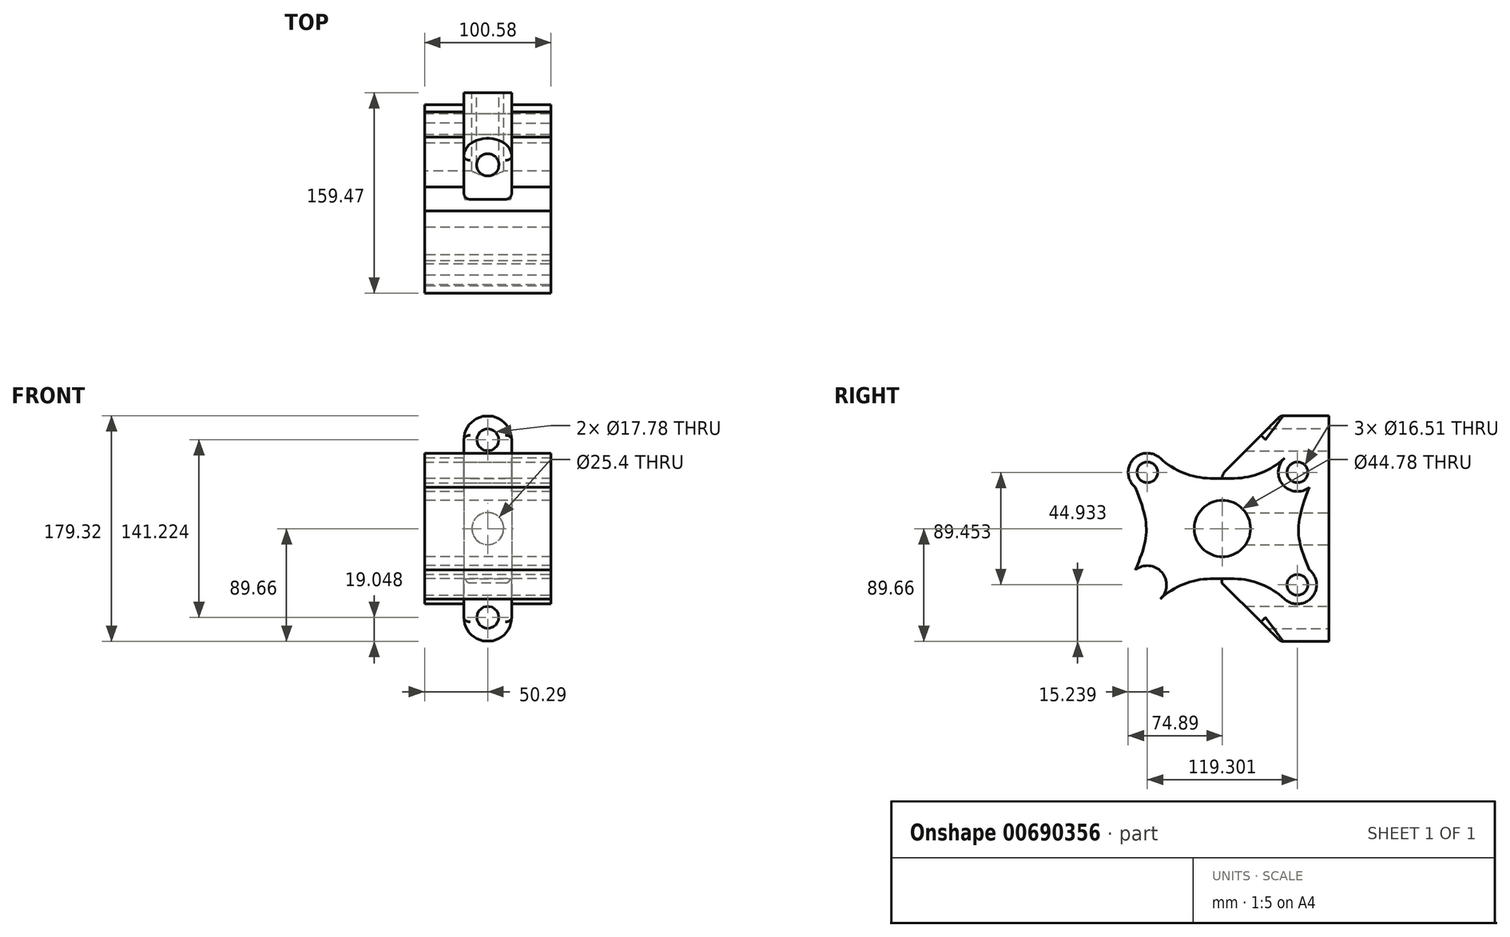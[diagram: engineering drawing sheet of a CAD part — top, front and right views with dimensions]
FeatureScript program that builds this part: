
annotation { "Feature Type Name" : "Feature", "Feature Type Description" : "" }
export const myFeature = defineFeature(function(context is Context, id is Id, definition is map)
    precondition{}
    {
        {
            var Q0;
            Q0=qCreatedBy(makeId("Right.planeOp"),FACE);
            var sketch = newSketch(context, id + "F0", { "sketchPlane" : qUnion([Q0])});
            skCircle(sketch, "E0", {"center": v(-59.65, 44.73) * mm, "radius": 15.24 * mm});
            skCircle(sketch, "E1.MirrorC", {"center": v(59.65, 44.73) * mm, "radius": 15.24 * mm});
            skCircle(sketch, "E2.MirrorC", {"center": v(59.65, -44.73) * mm, "radius": 15.24 * mm});
            skCircle(sketch, "E3.MirrorC", {"center": v(-59.65, -44.73) * mm, "radius": 15.24 * mm});
            skCircle(sketch, "E4", {"center": v(0, 0) * mm, "radius": 28.6 * mm});
            skCircle(sketch, "E5", {"center": v(0, 0) * mm, "radius": 22.4 * mm});
            skLineSegment(sketch, "E6.top", {"start": v(-9.5, 39.93) * mm, "end": v(15.9, 39.93) * mm});
            skArc(sketch, "E7", {"start": v(-49.3, 55.92) * mm, "mid": v(-30.87, 44.26) * mm, "end": v(-9.5, 39.93) * mm});
            skArc(sketch, "E8.MirrorCS", {"start": v(49.3, 55.92) * mm, "mid": v(30.87, 44.26) * mm, "end": v(9.5, 39.93) * mm});
            skArc(sketch, "E9.MirrorCS", {"start": v(49.3, -55.92) * mm, "mid": v(30.87, -44.26) * mm, "end": v(9.5, -39.93) * mm});
            skLineSegment(sketch, "E10.MirrorCS", {"start": v(-9.5, -39.93) * mm, "end": v(15.9, -39.93) * mm});
            skArc(sketch, "E11.MirrorCS", {"start": v(-49.3, -55.92) * mm, "mid": v(-30.87, -44.26) * mm, "end": v(-9.5, -39.93) * mm});
            skFitSpline(sketch, "E12", {"points": [v(69.2, 32.85) * mm, v(69.2, -32.84) * mm], "startDerivative": vector(-36.22, -89.62) * mm, "endDerivative": vector(33.53, -77.58) * mm});
            skFitSpline(sketch, "E13.MirrorCS", {"points": [v(-69.2, 32.85) * mm, v(-69.2, -32.84) * mm], "startDerivative": vector(36.22, -89.62) * mm, "endDerivative": vector(-33.53, -77.58) * mm});
            skPoint(sketch, "E6.left.start.orphan", {"position": v(-12.7, 65.76) * mm});
            skSolve(sketch);
        }
        {
            var Q0;
            Q0=qCreatedBy(makeId("Front.planeOp"),FACE);
            cPlane(context, id + "F1", {"entities" : qUnion([Q0]), "cplaneType" : CPlaneType.OFFSET, "offset" : 84.58 * mm, "oppositeDirection" : true, "width" : 152.4 * mm, "height" : 152.4 * mm});
        }
        {
            var Q0;
            Q0=qCreatedBy(id+"F1.planeOp",FACE);
            var sketch = newSketch(context, id + "F2", { "sketchPlane" : qUnion([Q0])});
            skArc(sketch, "E14", {"start": v(19.05, 70.61) * mm, "mid": v(0, 89.66) * mm, "end": v(-19.05, 70.61) * mm});
            skCircle(sketch, "E15", {"center": v(0, 0) * mm, "radius": 12.7 * mm});
            skArc(sketch, "E16", {"start": v(-19.05, -70.61) * mm, "mid": v(0, -89.66) * mm, "end": v(19.05, -70.61) * mm});
            skLineSegment(sketch, "E17", {"start": v(19.05, 70.61) * mm, "end": v(19.05, -70.61) * mm});
            skLineSegment(sketch, "E18", {"start": v(-19.05, 70.61) * mm, "end": v(-19.05, -70.61) * mm});
            skCircle(sketch, "E19", {"center": v(0, 70.61) * mm, "radius": 8.9 * mm});
            skCircle(sketch, "E20", {"center": v(0, -70.61) * mm, "radius": 8.9 * mm});
            skSolve(sketch);
        }
        {
            var Q0;
            Q0=makeQuery(id+"F0.imprint","IMPRINT",FACE,{"disambiguationData":[TD([[makeQuery(id+"F0.imprint","IMPRINT",EDGE,{"derivedFrom":sQuery(id+"F0.wireOp",EDGE,"E4")}),-1.0]])]});
            var Q1;
            {var subQ0=sQuery(id+"F0.wireOp",EDGE,"E0");var subQ1=makeQuery(id+"F0.imprint","INTERSECT",VERTEX,{"derivedFrom":[subQ0,sQuery(id+"F0.wireOp",EDGE,"E7")]});Q1=makeQuery(id+"F0.imprint","IMPRINT",FACE,{"disambiguationData":[TD([[makeQuery(id+"F0.imprint","IMPRINT",EDGE,{"disambiguationData":[TD([[subQ1,-1.0]])],"derivedFrom":subQ0}),1.0]])]});}
            var Q2;
            {var subQ0=sQuery(id+"F0.wireOp",EDGE,"E3.MirrorC");var subQ1=makeQuery(id+"F0.imprint","INTERSECT",VERTEX,{"derivedFrom":[subQ0,sQuery(id+"F0.wireOp",EDGE,"E11.MirrorCS")]});Q2=makeQuery(id+"F0.imprint","IMPRINT",FACE,{"disambiguationData":[TD([[makeQuery(id+"F0.imprint","IMPRINT",EDGE,{"disambiguationData":[TD([[subQ1,-1.0]])],"derivedFrom":subQ0}),-1.0]])]});}
            var Q3;
            {var subQ0=sQuery(id+"F0.wireOp",EDGE,"E1.MirrorC");var subQ1=makeQuery(id+"F0.imprint","INTERSECT",VERTEX,{"derivedFrom":[subQ0,sQuery(id+"F0.wireOp",EDGE,"E8.MirrorCS")]});Q3=makeQuery(id+"F0.imprint","IMPRINT",FACE,{"disambiguationData":[TD([[makeQuery(id+"F0.imprint","IMPRINT",EDGE,{"disambiguationData":[TD([[subQ1,-1.0]])],"derivedFrom":subQ0}),-1.0]])]});}
            var Q4;
            {var subQ0=sQuery(id+"F0.wireOp",EDGE,"E2.MirrorC");var subQ1=makeQuery(id+"F0.imprint","INTERSECT",VERTEX,{"derivedFrom":[sQuery(id+"F0.wireOp",EDGE,"E9.MirrorCS"),subQ0]});Q4=makeQuery(id+"F0.imprint","IMPRINT",FACE,{"disambiguationData":[TD([[makeQuery(id+"F0.imprint","IMPRINT",EDGE,{"disambiguationData":[TD([[subQ1,-1.0]])],"derivedFrom":subQ0}),1.0]])]});}
            var Q5;
            Q5=makeQuery(id+"F0.imprint","IMPRINT",FACE,{"disambiguationData":[TD([[makeQuery(id+"F0.imprint","IMPRINT",EDGE,{"derivedFrom":sQuery(id+"F0.wireOp",EDGE,"E4")}),1.0]])]});
            extrude(context, id + "F3", {"entities" : qUnion([Q0, Q1, Q2, Q3, Q4, Q5]), "endBound" : BoundingType.SYMMETRIC, "depth" : 100.58 * mm, "offsetDistance" : 25.4 * mm});
        }
        {
            var Q0;
            Q0=makeQuery(id+"F2.imprint","IMPRINT",FACE,{"disambiguationData":[TD([[makeQuery(id+"F2.imprint","IMPRINT",EDGE,{"derivedFrom":sQuery(id+"F2.wireOp",EDGE,"E14")}),1.0]])]});
            extrude(context, id + "F4", {"entities" : qUnion([Q0]), "operationType" : NewBodyOperationType.ADD, "depth" : 84.84 * mm, "offsetDistance" : 25.4 * mm});
        }
        {
            var Q0;
            Q0=qCreatedBy(makeId("Right.planeOp"),FACE);
            var sketch = newSketch(context, id + "F5", { "sketchPlane" : qUnion([Q0])});
            skLineSegment(sketch, "E21", {"start": v(-2.45, 41) * mm, "end": v(-2.45, 96.5) * mm});
            skLineSegment(sketch, "E22", {"start": v(-2.45, 96.5) * mm, "end": v(53.05, 96.5) * mm});
            skLineSegment(sketch, "E23", {"start": v(53.05, 96.5) * mm, "end": v(-2.45, 41) * mm});
            skLineSegment(sketch, "E24", {"start": v(0, 0) * mm, "end": v(98.04, 0) * mm, "construction": true});
            skLineSegment(sketch, "E25.MirrorCS", {"start": v(-2.45, -41) * mm, "end": v(-2.45, -96.5) * mm});
            skLineSegment(sketch, "E26.MirrorCS", {"start": v(53.05, -96.5) * mm, "end": v(-2.45, -41) * mm});
            skLineSegment(sketch, "E27.MirrorCS", {"start": v(-2.45, -96.5) * mm, "end": v(53.05, -96.5) * mm});
            skSolve(sketch);
        }
        {
            var Q0;
            Q0=makeQuery(id+"F5.imprint","IMPRINT",FACE,{"disambiguationData":[TD([[makeQuery(id+"F5.imprint","IMPRINT",EDGE,{"derivedFrom":sQuery(id+"F5.wireOp",EDGE,"E21")}),-1.0]])]});
            var Q1;
            Q1=makeQuery(id+"F5.imprint","IMPRINT",FACE,{"disambiguationData":[TD([[makeQuery(id+"F5.imprint","IMPRINT",EDGE,{"derivedFrom":sQuery(id+"F5.wireOp",EDGE,"E25.MirrorCS")}),1.0]])]});
            extrude(context, id + "F6", {"entities" : qUnion([Q0, Q1]), "operationType" : NewBodyOperationType.REMOVE, "endBound" : BoundingType.SYMMETRIC, "oppositeDirection" : true, "depth" : 101.6 * mm, "offsetDistance" : 25.4 * mm});
        }
        {
            var Q0;
            Q0=makeQuery(id+"F3.opExtrude","CAP_FACE",FACE,{"disambiguationData":[OSD([sQuery(id+"F0.wireOp",EDGE,"E0"),sQuery(id+"F0.wireOp",EDGE,"E1.MirrorC"),sQuery(id+"F0.wireOp",EDGE,"E5"),sQuery(id+"F0.wireOp",EDGE,"E6.top"),sQuery(id+"F0.wireOp",EDGE,"E7"),sQuery(id+"F0.wireOp",EDGE,"E8.MirrorCS"),sQuery(id+"F0.wireOp",EDGE,"E9.MirrorCS"),sQuery(id+"F0.wireOp",EDGE,"E10.MirrorCS"),sQuery(id+"F0.wireOp",EDGE,"E2.MirrorC"),sQuery(id+"F0.wireOp",EDGE,"E3.MirrorC"),sQuery(id+"F0.wireOp",EDGE,"E11.MirrorCS"),sQuery(id+"F0.wireOp",EDGE,"E12"),sQuery(id+"F0.wireOp",EDGE,"E13.MirrorCS")])],"isStart":false});
            var sketch = newSketch(context, id + "F7", { "sketchPlane" : qUnion([Q0])});
            skSolve(sketch);
        }
        {
            var Q0;
            Q0=makeQuery(id+"F3.opExtrude","CAP_FACE",FACE,{"disambiguationData":[OSD([sQuery(id+"F0.wireOp",EDGE,"E0"),sQuery(id+"F0.wireOp",EDGE,"E1.MirrorC"),sQuery(id+"F0.wireOp",EDGE,"E5"),sQuery(id+"F0.wireOp",EDGE,"E6.top"),sQuery(id+"F0.wireOp",EDGE,"E7"),sQuery(id+"F0.wireOp",EDGE,"E8.MirrorCS"),sQuery(id+"F0.wireOp",EDGE,"E9.MirrorCS"),sQuery(id+"F0.wireOp",EDGE,"E10.MirrorCS"),sQuery(id+"F0.wireOp",EDGE,"E2.MirrorC"),sQuery(id+"F0.wireOp",EDGE,"E3.MirrorC"),sQuery(id+"F0.wireOp",EDGE,"E11.MirrorCS"),sQuery(id+"F0.wireOp",EDGE,"E12"),sQuery(id+"F0.wireOp",EDGE,"E13.MirrorCS")])],"isStart":true});
            var sketch = newSketch(context, id + "F8", { "sketchPlane" : qUnion([Q0])});
            skCircle(sketch, "E28", {"center": v(-59.65, -44.73) * mm, "radius": 8.26 * mm});
            skCircle(sketch, "E29", {"center": v(-59.65, 44.73) * mm, "radius": 8.26 * mm});
            skCircle(sketch, "E30", {"center": v(59.65, 44.73) * mm, "radius": 8.26 * mm});
            skCircle(sketch, "E31", {"center": v(59.65, -44.73) * mm, "radius": 8.26 * mm});
            skCircle(sketch, "E32", {"center": v(0, 0) * mm, "radius": 24.23 * mm});
            skSolve(sketch);
        }
        {
            var Q0;
            Q0=makeQuery(id+"F8.imprint","IMPRINT",FACE,{"disambiguationData":[TD([[makeQuery(id+"F8.imprint","IMPRINT",EDGE,{"derivedFrom":sQuery(id+"F8.wireOp",EDGE,"E29")}),1.0]])]});
            var Q1;
            Q1=makeQuery(id+"F8.imprint","IMPRINT",FACE,{"disambiguationData":[TD([[makeQuery(id+"F8.imprint","IMPRINT",EDGE,{"derivedFrom":sQuery(id+"F8.wireOp",EDGE,"E28")}),1.0]])]});
            var Q2;
            Q2=makeQuery(id+"F8.imprint","IMPRINT",FACE,{"disambiguationData":[TD([[makeQuery(id+"F8.imprint","IMPRINT",EDGE,{"derivedFrom":sQuery(id+"F8.wireOp",EDGE,"E31")}),1.0]])]});
            var Q3;
            Q3=makeQuery(id+"F8.imprint","IMPRINT",FACE,{"disambiguationData":[TD([[makeQuery(id+"F8.imprint","IMPRINT",EDGE,{"derivedFrom":sQuery(id+"F8.wireOp",EDGE,"E30")}),1.0]])]});
            extrude(context, id + "F9", {"entities" : qUnion([Q0, Q1, Q2, Q3]), "operationType" : NewBodyOperationType.REMOVE, "endBound" : BoundingType.SYMMETRIC, "depth" : 203.2 * mm, "offsetDistance" : 25.4 * mm});
        }
        {
            var Q0;
            {var subQ0=sQuery(id+"F2.wireOp",EDGE,"E18");Q0=makeQuery(id+"F4.boolean.opBoolean","SPLIT",FACE,{"disambiguationData":[TD([makeQuery(id+"F3.opExtrude","SWEPT_FACE",FACE,{"disambiguationData":[OSD([sQuery(id+"F0.wireOp",EDGE,"E5")])]})])],"derivedFrom":makeQuery(id+"F4.opExtrude","SWEPT_FACE",FACE,{"disambiguationData":[OSD([subQ0])]})});}
            extrude(context, id + "F10", {"entities" : qUnion([Q0]), "operationType" : NewBodyOperationType.REMOVE, "endBound" : BoundingType.SYMMETRIC, "oppositeDirection" : true, "depth" : 203.2 * mm, "offsetDistance" : 25.4 * mm});
        }
        {
            var Q0;
            {var subQ0=sQuery(id+"F2.wireOp",EDGE,"E18");var subQ1=sQuery(id+"F2.wireOp",EDGE,"E17");var subQ2=sQuery(id+"F2.wireOp",EDGE,"E14");var subQ3=sQuery(id+"F2.wireOp",EDGE,"E19");Q0=makeQuery(id+"F6.boolean.opBoolean","INTERSECT",EDGE,{"derivedFrom":[makeQuery(id+"F4.boolean.opBoolean","SPLIT",FACE,{"disambiguationData":[TD([makeQuery(id+"F3.opExtrude","SWEPT_FACE",FACE,{"disambiguationData":[OSD([sQuery(id+"F0.wireOp",EDGE,"E6.top")])]})])],"derivedFrom":makeQuery(id+"F4.opExtrude","CAP_FACE",FACE,{"disambiguationData":[OSD([subQ2,sQuery(id+"F2.wireOp",EDGE,"E15"),sQuery(id+"F2.wireOp",EDGE,"E16"),subQ1,subQ0,subQ3,sQuery(id+"F2.wireOp",EDGE,"E20")])],"isStart":false})}),makeQuery(id+"F6.opExtrude","SWEPT_FACE",FACE,{"disambiguationData":[OSD([sQuery(id+"F5.wireOp",EDGE,"E23")])]})]});}
            fillet(context, id + "F11", {"entities" : qUnion([Q0]), "radius" : 10.16 * mm, "tangentPropagation" : true, "allowEdgeOverflow" : false});
        }
        {
            var Q0;
            {var subQ3=sQuery(id+"F2.wireOp",EDGE,"E17");Q0=makeQuery(id+"F6.boolean.opBoolean","INTERSECT",EDGE,{"derivedFrom":[makeQuery(id+"F4.boolean.opBoolean","SPLIT",FACE,{"disambiguationData":[TD([makeQuery(id+"F3.opExtrude","SWEPT_FACE",FACE,{"disambiguationData":[OSD([sQuery(id+"F0.wireOp",EDGE,"E1.MirrorC")])]})])],"derivedFrom":makeQuery(id+"F4.opExtrude","SWEPT_FACE",FACE,{"disambiguationData":[OSD([subQ3])]})}),makeQuery(id+"F6.opExtrude","SWEPT_FACE",FACE,{"disambiguationData":[OSD([sQuery(id+"F5.wireOp",EDGE,"E23")])]})]});}
            var Q1;
            Q1=makeQuery(id+"F6.boolean.opBoolean","INTERSECT",EDGE,{"derivedFrom":[makeQuery(id+"F4.opExtrude","SWEPT_FACE",FACE,{"disambiguationData":[OSD([sQuery(id+"F2.wireOp",EDGE,"E14")])]}),makeQuery(id+"F6.opExtrude","SWEPT_FACE",FACE,{"disambiguationData":[OSD([sQuery(id+"F5.wireOp",EDGE,"E23")])]})]});
            var Q2;
            {var subQ2=sQuery(id+"F2.wireOp",EDGE,"E18");Q2=makeQuery(id+"F6.boolean.opBoolean","INTERSECT",EDGE,{"derivedFrom":[makeQuery(id+"F4.boolean.opBoolean","SPLIT",FACE,{"disambiguationData":[TD([makeQuery(id+"F3.opExtrude","SWEPT_FACE",FACE,{"disambiguationData":[OSD([sQuery(id+"F0.wireOp",EDGE,"E1.MirrorC")])]})])],"derivedFrom":makeQuery(id+"F4.opExtrude","SWEPT_FACE",FACE,{"disambiguationData":[OSD([subQ2])]})}),makeQuery(id+"F6.opExtrude","SWEPT_FACE",FACE,{"disambiguationData":[OSD([sQuery(id+"F5.wireOp",EDGE,"E26.MirrorCS")])]})]});}
            var Q3;
            Q3=makeQuery(id+"F6.boolean.opBoolean","INTERSECT",EDGE,{"derivedFrom":[makeQuery(id+"F4.opExtrude","SWEPT_FACE",FACE,{"disambiguationData":[OSD([sQuery(id+"F2.wireOp",EDGE,"E16")])]}),makeQuery(id+"F6.opExtrude","SWEPT_FACE",FACE,{"disambiguationData":[OSD([sQuery(id+"F5.wireOp",EDGE,"E26.MirrorCS")])]})]});
            var Q4;
            {var subQ3=sQuery(id+"F2.wireOp",EDGE,"E17");Q4=makeQuery(id+"F6.boolean.opBoolean","INTERSECT",EDGE,{"derivedFrom":[makeQuery(id+"F4.boolean.opBoolean","SPLIT",FACE,{"disambiguationData":[TD([makeQuery(id+"F3.opExtrude","SWEPT_FACE",FACE,{"disambiguationData":[OSD([sQuery(id+"F0.wireOp",EDGE,"E1.MirrorC")])]})])],"derivedFrom":makeQuery(id+"F4.opExtrude","SWEPT_FACE",FACE,{"disambiguationData":[OSD([subQ3])]})}),makeQuery(id+"F6.opExtrude","SWEPT_FACE",FACE,{"disambiguationData":[OSD([sQuery(id+"F5.wireOp",EDGE,"E26.MirrorCS")])]})]});}
            fillet(context, id + "F12", {"entities" : qUnion([Q0, Q1, Q2, Q3, Q4]), "radius" : 5.08 * mm, "tangentPropagation" : true, "allowEdgeOverflow" : false});
        }
        {
            var Q0;
            Q0=qCreatedBy(id+"F1.planeOp",FACE);
            var sketch = newSketch(context, id + "F13", { "sketchPlane" : qUnion([Q0])});
            skCircle(sketch, "E33", {"center": v(0, 0) * mm, "radius": 12.7 * mm});
            skSolve(sketch);
        }
        {
            var Q0;
            Q0=makeQuery(id+"F13.imprint","IMPRINT",FACE,{"disambiguationData":[TD([[makeQuery(id+"F13.imprint","IMPRINT",EDGE,{"derivedFrom":sQuery(id+"F13.wireOp",EDGE,"E33")}),1.0]])]});
            extrude(context, id + "F14", {"entities" : qUnion([Q0]), "operationType" : NewBodyOperationType.REMOVE, "endBound" : BoundingType.SYMMETRIC, "oppositeDirection" : true, "depth" : 152.4 * mm, "offsetDistance" : 25.4 * mm});
        }
    });
